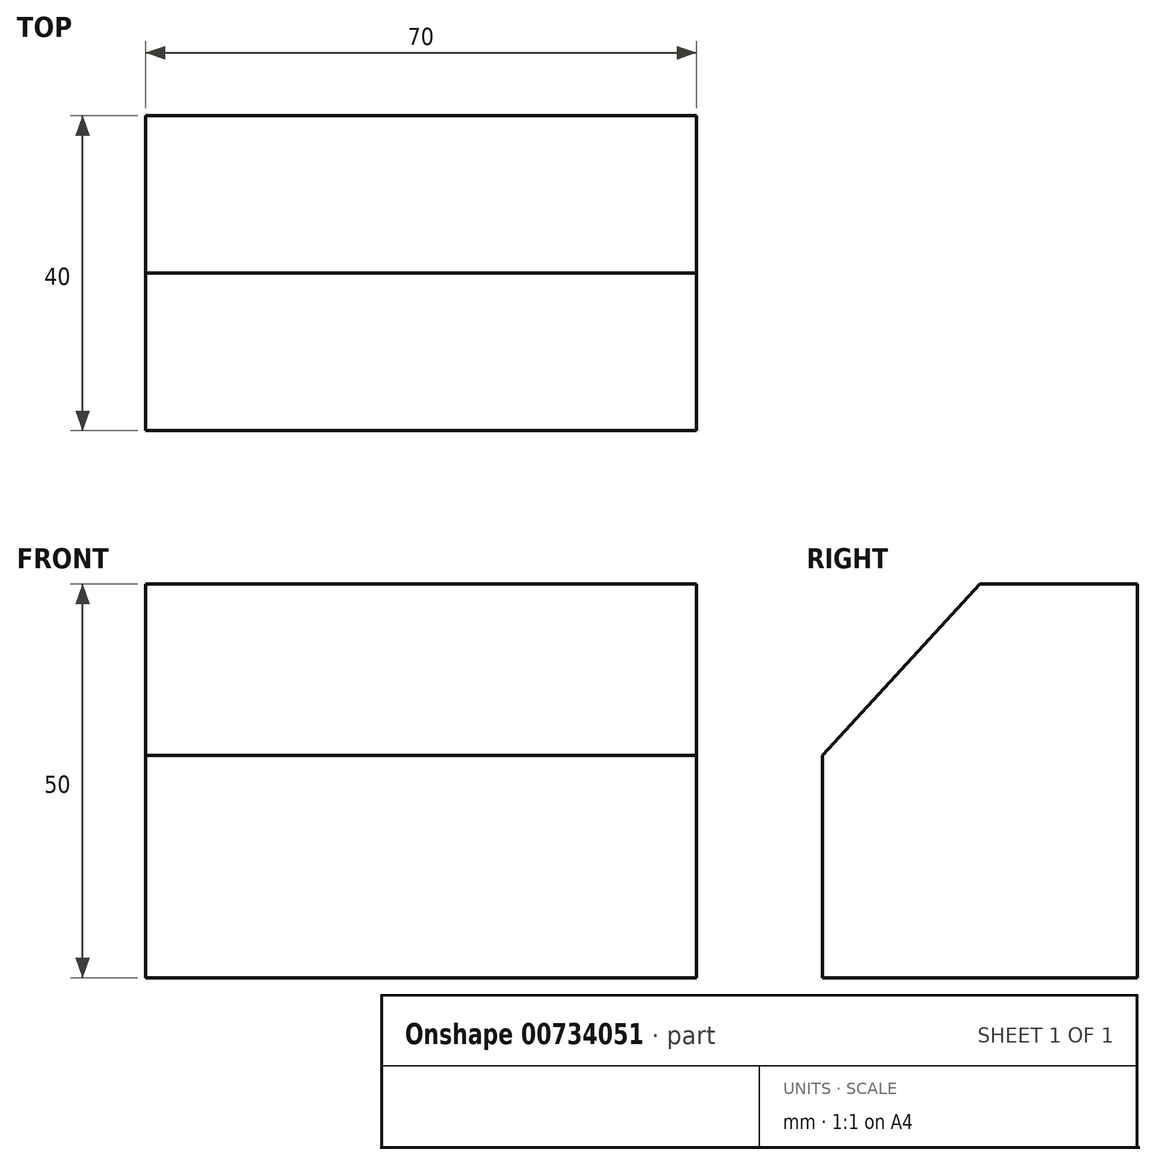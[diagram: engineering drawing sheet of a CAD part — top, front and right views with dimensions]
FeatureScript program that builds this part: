
annotation { "Feature Type Name" : "Feature", "Feature Type Description" : "" }
export const myFeature = defineFeature(function(context is Context, id is Id, definition is map)
    precondition{}
    {
        {
            var Q0;
            Q0=qCreatedBy(makeId("Front.planeOp"),FACE);
            var sketch = newSketch(context, id + "F0", { "sketchPlane" : qUnion([Q0])});
            skLineSegment(sketch, "E0.bottom", {"start": v(0, 0) * mm, "end": v(70, 0) * mm});
            skLineSegment(sketch, "E0.top", {"start": v(0, 50) * mm, "end": v(70, 50) * mm});
            skLineSegment(sketch, "E0.left", {"start": v(0, 0) * mm, "end": v(0, 50) * mm});
            skLineSegment(sketch, "E0.right", {"start": v(70, 0) * mm, "end": v(70, 50) * mm});
            skSolve(sketch);
        }
        {
            var Q0;
            Q0 = qSketchRegion(id + "F0", true);
            extrude(context, id + "F1", {"entities" : qUnion([Q0]), "depth" : 40 * mm, "offsetDistance" : 25 * mm});
        }
        {
            var Q0;
            Q0=makeQuery(id+"F1.opExtrude","SWEPT_FACE",FACE,{"disambiguationData":[OSD([sQuery(id+"F0.wireOp",EDGE,"E0.right")])]});
            var sketch = newSketch(context, id + "F2", { "sketchPlane" : qUnion([Q0])});
            skLineSegment(sketch, "E1", {"start": v(-40, 28.24) * mm, "end": v(-20, 50) * mm});
            skLineSegment(sketch, "E2", {"start": v(-20, 50) * mm, "end": v(-40, 50) * mm});
            skLineSegment(sketch, "E3", {"start": v(-40, 50) * mm, "end": v(-40, 28.24) * mm});
            skSolve(sketch);
        }
        {
            var Q0;
            Q0 = qSketchRegion(id + "F2", true);
            extrude(context, id + "F3", {"entities" : qUnion([Q0]), "operationType" : NewBodyOperationType.REMOVE, "endBound" : BoundingType.THROUGH_ALL, "oppositeDirection" : true, "depth" : 25 * mm, "offsetDistance" : 25 * mm});
        }
    });
